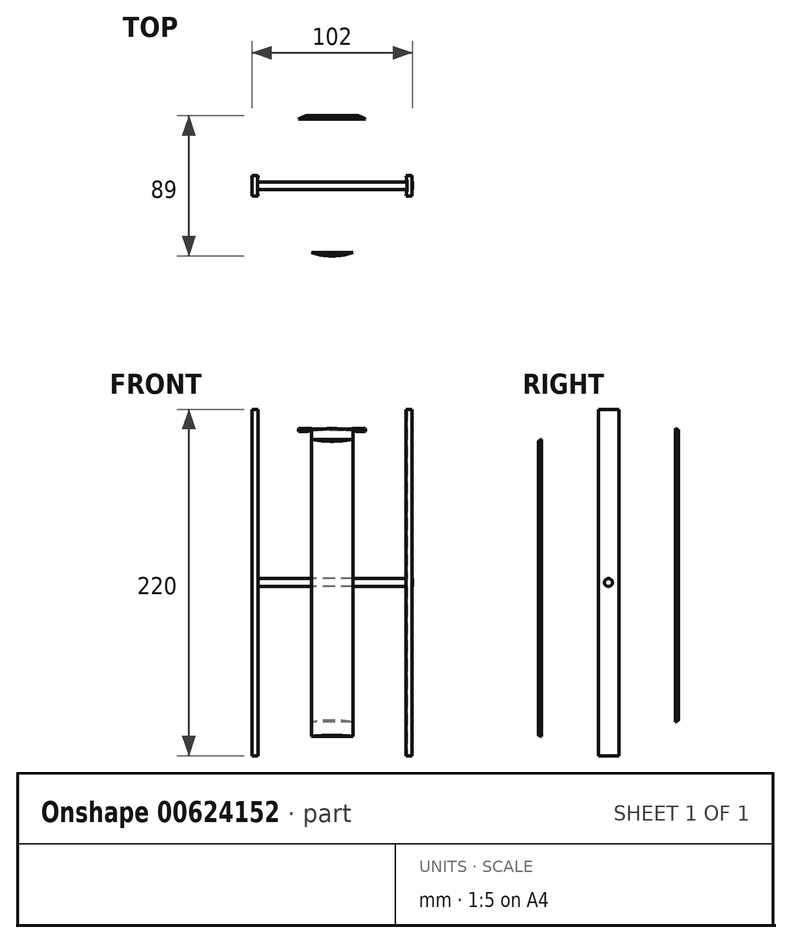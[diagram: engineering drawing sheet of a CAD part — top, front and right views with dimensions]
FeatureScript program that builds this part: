
annotation { "Feature Type Name" : "Feature", "Feature Type Description" : "" }
export const myFeature = defineFeature(function(context is Context, id is Id, definition is map)
    precondition{}
    {
        {
            var Q0;
            Q0=qCreatedBy(makeId("Right.planeOp"),FACE);
            var sketch = newSketch(context, id + "F0", { "sketchPlane" : qUnion([Q0])});
            skLineSegment(sketch, "E0", {"start": v(0, 120.05) * mm, "end": v(0, -127.77) * mm, "construction": true});
            skLineSegment(sketch, "E1", {"start": v(-143.58, 0) * mm, "end": v(127.4, 0) * mm, "construction": true});
            skArc(sketch, "E2", {"start": v(-57.5, 85.46) * mm, "mid": v(-11.29, 102.38) * mm, "end": v(37.5, 95.93) * mm});
            skArc(sketch, "E3.0", {"start": v(-57.5, 87.86) * mm, "mid": v(-11.23, 104.4) * mm, "end": v(37.5, 98.08) * mm});
            skLineSegment(sketch, "E4", {"start": v(-10, -19.22) * mm, "end": v(-10, 530.31) * mm, "construction": true});
            skCircle(sketch, "E5", {"center": v(-10, 215.8) * mm, "radius": 47.5 * mm});
            skLineSegment(sketch, "E6", {"start": v(37.5, -87.86) * mm, "end": v(37.5, -85.46) * mm});
            skLineSegment(sketch, "E7", {"start": v(-57.5, -98.08) * mm, "end": v(-57.5, -95.93) * mm});
            skLineSegment(sketch, "E8", {"start": v(-20, 37.4) * mm, "end": v(-20, -41.37) * mm, "construction": true});
            skArc(sketch, "E9", {"start": v(-57.5, -95.93) * mm, "mid": v(-8.71, -102.38) * mm, "end": v(37.5, -85.46) * mm});
            skArc(sketch, "E10.0", {"start": v(-57.5, -98.08) * mm, "mid": v(-8.77, -104.4) * mm, "end": v(37.5, -87.86) * mm});
            skLineSegment(sketch, "E11", {"start": v(37.5, 104.3) * mm, "end": v(37.5, 301.45) * mm, "construction": true});
            skLineSegment(sketch, "E12", {"start": v(-57.5, 94.09) * mm, "end": v(-57.5, 324.59) * mm, "construction": true});
            skLineSegment(sketch, "E13.trimOffspring", {"start": v(-57.5, 85.46) * mm, "end": v(-57.5, 87.86) * mm});
            skLineSegment(sketch, "E14.trimOffspring", {"start": v(37.5, 95.93) * mm, "end": v(37.5, 98.08) * mm});
            skLineSegment(sketch, "E15", {"start": v(34.5, 97.05) * mm, "end": v(34.5, -87.4) * mm});
            skLineSegment(sketch, "E16", {"start": v(-54.5, 87.4) * mm, "end": v(-54.5, -97.05) * mm});
            skPoint(sketch, "E17.orphan", {"position": v(34.5, 53.9) * mm});
            skPoint(sketch, "E18.orphan", {"position": v(-54.5, 49.75) * mm});
            skLineSegment(sketch, "E19", {"start": v(34.5, -87.4) * mm, "end": v(34.5, -118.04) * mm});
            skLineSegment(sketch, "E20", {"start": v(34.5, -118.04) * mm, "end": v(-54.5, -118.04) * mm});
            skLineSegment(sketch, "E21", {"start": v(-54.5, -118.04) * mm, "end": v(-54.5, -97.05) * mm});
            skLineSegment(sketch, "E22", {"start": v(-54.5, 87.4) * mm, "end": v(-54.5, 114.95) * mm});
            skLineSegment(sketch, "E23", {"start": v(-54.5, 114.95) * mm, "end": v(34.5, 114.95) * mm});
            skLineSegment(sketch, "E24", {"start": v(34.5, 114.95) * mm, "end": v(34.5, 97.05) * mm});
            skLineSegment(sketch, "E25.0", {"start": v(32.5, 114.95) * mm, "end": v(32.5, -118.04) * mm});
            skLineSegment(sketch, "E26.0", {"start": v(-52.5, 114.95) * mm, "end": v(-52.5, -118.04) * mm});
            skCircle(sketch, "E27", {"center": v(-10, 0) * mm, "radius": 2.5 * mm});
            skSolve(sketch);
        }
        {
            var Q0;
            Q0=makeQuery(id+"F0.imprint","IMPRINT",FACE,{"disambiguationData":[TD([[makeQuery(id+"F0.imprint","IMPRINT",EDGE,{"derivedFrom":sQuery(id+"F0.wireOp",EDGE,"E3.0")}),-1.0]])]});
            var Q1;
            {var subQ4=sQuery(id+"F0.wireOp",EDGE,"E6");Q1=makeQuery(id+"F0.imprint","IMPRINT",FACE,{"disambiguationData":[TD([[makeQuery(id+"F0.imprint","IMPRINT",EDGE,{"derivedFrom":subQ4}),1.0]])]});}
            var Q2;
            {var subQ0=sQuery(id+"F0.wireOp",EDGE,"E19");var subQ5=sQuery(id+"F0.wireOp",EDGE,"E10.0");var subQ6=makeQuery(id+"F0.imprint","INTERSECT",VERTEX,{"derivedFrom":[subQ5,subQ0]});Q2=makeQuery(id+"F0.imprint","IMPRINT",FACE,{"disambiguationData":[TD([[makeQuery(id+"F0.imprint","IMPRINT",EDGE,{"disambiguationData":[TD([[subQ6,1.0]])],"derivedFrom":subQ5}),1.0]])]});}
            var Q3;
            {var subQ0=sQuery(id+"F0.wireOp",EDGE,"E26.0");var subQ1=sQuery(id+"F0.wireOp",EDGE,"E9");var subQ2=makeQuery(id+"F0.imprint","INTERSECT",VERTEX,{"derivedFrom":[subQ1,subQ0]});Q3=makeQuery(id+"F0.imprint","IMPRINT",FACE,{"disambiguationData":[TD([[makeQuery(id+"F0.imprint","IMPRINT",EDGE,{"disambiguationData":[TD([[subQ2,-1.0]])],"derivedFrom":subQ1}),-1.0]])]});}
            var Q4;
            {var subQ0=sQuery(id+"F0.wireOp",EDGE,"E7");Q4=makeQuery(id+"F0.imprint","IMPRINT",FACE,{"disambiguationData":[TD([[makeQuery(id+"F0.imprint","IMPRINT",EDGE,{"derivedFrom":subQ0}),-1.0]])]});}
            var Q5;
            {var subQ0=sQuery(id+"F0.wireOp",EDGE,"E21");var subQ5=sQuery(id+"F0.wireOp",EDGE,"E10.0");var subQ6=makeQuery(id+"F0.imprint","INTERSECT",VERTEX,{"derivedFrom":[subQ5,subQ0]});Q5=makeQuery(id+"F0.imprint","IMPRINT",FACE,{"disambiguationData":[TD([[makeQuery(id+"F0.imprint","IMPRINT",EDGE,{"disambiguationData":[TD([[subQ6,-1.0]])],"derivedFrom":subQ5}),1.0]])]});}
            extrude(context, id + "F1", {"entities" : qUnion([Q0, Q1, Q2, Q3, Q4, Q5]), "endBound" : BoundingType.SYMMETRIC, "depth" : 100 * mm, "offsetDistance" : 25 * mm});
        }
        {
            var Q0;
            Q0=qCreatedBy(makeId("Top.planeOp"),FACE);
            var sketch = newSketch(context, id + "F2", { "sketchPlane" : qUnion([Q0])});
            skLineSegment(sketch, "E28.0", {"start": v(0, 37.5) * mm, "end": v(0, -57.5) * mm, "construction": true});
            skCircle(sketch, "E29", {"center": v(0, -10) * mm, "radius": 47.5 * mm});
            skLineSegment(sketch, "E30.bottom", {"start": v(-50.85, -16.52) * mm, "end": v(50.85, -16.52) * mm});
            skLineSegment(sketch, "E30.top", {"start": v(-50.85, -3.48) * mm, "end": v(50.85, -3.48) * mm});
            skLineSegment(sketch, "E30.left", {"start": v(-50.85, -16.52) * mm, "end": v(-50.85, -3.48) * mm});
            skLineSegment(sketch, "E30.right", {"start": v(50.85, -16.52) * mm, "end": v(50.85, -3.48) * mm});
            skSolve(sketch);
        }
        {
            var Q0;
            Q0=makeQuery(id+"F2.imprint","IMPRINT",FACE,{"disambiguationData":[TD([[makeQuery(id+"F2.imprint","IMPRINT",EDGE,{"derivedFrom":sQuery(id+"F2.wireOp",EDGE,"E29")}),1.0]])]});
            var Q1;
            {var subQ0=sQuery(id+"F2.wireOp",EDGE,"E30.bottom");var subQ1=sQuery(id+"F2.wireOp",EDGE,"E29");var subQ2=makeQuery(id+"F2.imprint","INTERSECT",VERTEX,{"disambiguationData":[OD(0.0)],"derivedFrom":[subQ1,subQ0]});Q1=makeQuery(id+"F2.imprint","IMPRINT",FACE,{"disambiguationData":[TD([[makeQuery(id+"F2.imprint","IMPRINT",EDGE,{"disambiguationData":[TD([[subQ2,-1.0]])],"derivedFrom":subQ1}),1.0]])]});}
            var Q2;
            {var subQ0=sQuery(id+"F2.wireOp",EDGE,"E30.top");var subQ1=sQuery(id+"F2.wireOp",EDGE,"E29");var subQ2=makeQuery(id+"F2.imprint","INTERSECT",VERTEX,{"disambiguationData":[OD(0.0)],"derivedFrom":[subQ1,subQ0]});Q2=makeQuery(id+"F2.imprint","IMPRINT",FACE,{"disambiguationData":[TD([[makeQuery(id+"F2.imprint","IMPRINT",EDGE,{"disambiguationData":[TD([[subQ2,1.0]])],"derivedFrom":subQ1}),1.0]])]});}
            extrude(context, id + "F3", {"entities" : qUnion([Q0, Q1, Q2]), "operationType" : NewBodyOperationType.INTERSECT, "endBound" : BoundingType.SYMMETRIC, "depth" : 300 * mm, "offsetDistance" : 25 * mm});
        }
        {
            var Q0;
            {var subQ0=sQuery(id+"F0.wireOp",EDGE,"E24");var subQ1=sQuery(id+"F0.wireOp",EDGE,"E3.0");var subQ2=makeQuery(id+"F0.imprint","INTERSECT",VERTEX,{"derivedFrom":[subQ1,subQ0]});Q0=makeQuery(id+"F0.imprint","IMPRINT",FACE,{"disambiguationData":[TD([[makeQuery(id+"F0.imprint","IMPRINT",EDGE,{"disambiguationData":[TD([[subQ2,1.0]])],"derivedFrom":subQ1}),1.0]])]});}
            var Q1;
            {var subQ0=sQuery(id+"F0.wireOp",EDGE,"E15");Q1=makeQuery(id+"F0.imprint","IMPRINT",FACE,{"disambiguationData":[TD([[makeQuery(id+"F0.imprint","IMPRINT",EDGE,{"derivedFrom":subQ0}),-1.0]])]});}
            var Q2;
            {var subQ0=sQuery(id+"F0.wireOp",EDGE,"E24");var subQ5=sQuery(id+"F0.wireOp",EDGE,"E3.0");var subQ6=makeQuery(id+"F0.imprint","INTERSECT",VERTEX,{"derivedFrom":[subQ5,subQ0]});Q2=makeQuery(id+"F0.imprint","IMPRINT",FACE,{"disambiguationData":[TD([[makeQuery(id+"F0.imprint","IMPRINT",EDGE,{"disambiguationData":[TD([[subQ6,1.0]])],"derivedFrom":subQ5}),-1.0]])]});}
            var Q3;
            {var subQ0=sQuery(id+"F0.wireOp",EDGE,"E19");var subQ5=sQuery(id+"F0.wireOp",EDGE,"E10.0");var subQ6=makeQuery(id+"F0.imprint","INTERSECT",VERTEX,{"derivedFrom":[subQ5,subQ0]});Q3=makeQuery(id+"F0.imprint","IMPRINT",FACE,{"disambiguationData":[TD([[makeQuery(id+"F0.imprint","IMPRINT",EDGE,{"disambiguationData":[TD([[subQ6,1.0]])],"derivedFrom":subQ5}),1.0]])]});}
            var Q4;
            {var subQ0=sQuery(id+"F0.wireOp",EDGE,"E19");var subQ1=sQuery(id+"F0.wireOp",EDGE,"E10.0");var subQ2=makeQuery(id+"F0.imprint","INTERSECT",VERTEX,{"derivedFrom":[subQ1,subQ0]});Q4=makeQuery(id+"F0.imprint","IMPRINT",FACE,{"disambiguationData":[TD([[makeQuery(id+"F0.imprint","IMPRINT",EDGE,{"disambiguationData":[TD([[subQ2,1.0]])],"derivedFrom":subQ1}),-1.0]])]});}
            var Q5;
            Q5=sQuery(id+"F0.wireOp",EDGE,"E4");
            revolve(context, id + "F4", {"entities" : qUnion([Q0, Q1, Q2, Q3, Q4]), "axis" : qUnion([Q5]), "revolveType" : RevolveType.FULL});
        }
        {
            var Q0;
            {var subQ0=sQuery(id+"F0.wireOp",EDGE,"E26.0");var subQ1=sQuery(id+"F0.wireOp",EDGE,"E2");var subQ2=makeQuery(id+"F0.imprint","INTERSECT",VERTEX,{"derivedFrom":[subQ1,subQ0]});Q0=makeQuery(id+"F0.imprint","IMPRINT",FACE,{"disambiguationData":[TD([[makeQuery(id+"F0.imprint","IMPRINT",EDGE,{"disambiguationData":[TD([[subQ2,-1.0]])],"derivedFrom":subQ1}),-1.0]])]});}
            var Q1;
            {var subQ0=sQuery(id+"F0.wireOp",EDGE,"E16");Q1=makeQuery(id+"F0.imprint","IMPRINT",FACE,{"disambiguationData":[TD([[makeQuery(id+"F0.imprint","IMPRINT",EDGE,{"derivedFrom":subQ0}),1.0]])]});}
            var Q2;
            {var subQ0=sQuery(id+"F0.wireOp",EDGE,"E15");Q2=makeQuery(id+"F0.imprint","IMPRINT",FACE,{"disambiguationData":[TD([[makeQuery(id+"F0.imprint","IMPRINT",EDGE,{"derivedFrom":subQ0}),-1.0]])]});}
            var Q3;
            Q3=makeQuery(id+"F0.imprint","IMPRINT",FACE,{"disambiguationData":[TD([[makeQuery(id+"F0.imprint","IMPRINT",EDGE,{"derivedFrom":sQuery(id+"F0.wireOp",EDGE,"E27")}),1.0]])]});
            extrude(context, id + "F5", {"entities" : qUnion([Q0, Q1, Q2, Q3]), "operationType" : NewBodyOperationType.INTERSECT, "endBound" : BoundingType.SYMMETRIC, "depth" : 100 * mm, "offsetDistance" : 25 * mm});
        }
        {
            var Q0;
            {var subQ5=sQuery(id+"F2.wireOp",EDGE,"E30.left");Q0=makeQuery(id+"F2.imprint","IMPRINT",FACE,{"disambiguationData":[TD([[makeQuery(id+"F2.imprint","IMPRINT",EDGE,{"derivedFrom":subQ5}),-1.0]])]});}
            var Q1;
            {var subQ5=sQuery(id+"F2.wireOp",EDGE,"E30.right");Q1=makeQuery(id+"F2.imprint","IMPRINT",FACE,{"disambiguationData":[TD([[makeQuery(id+"F2.imprint","IMPRINT",EDGE,{"derivedFrom":subQ5}),1.0]])]});}
            extrude(context, id + "F6", {"entities" : qUnion([Q0, Q1]), "operationType" : NewBodyOperationType.ADD, "endBound" : BoundingType.SYMMETRIC, "depth" : 220 * mm, "offsetDistance" : 25 * mm});
        }
        {
            var Q0;
            Q0=makeQuery(id+"F0.imprint","IMPRINT",FACE,{"disambiguationData":[TD([[makeQuery(id+"F0.imprint","IMPRINT",EDGE,{"derivedFrom":sQuery(id+"F0.wireOp",EDGE,"E27")}),1.0]])]});
            extrude(context, id + "F7", {"entities" : qUnion([Q0]), "operationType" : NewBodyOperationType.REMOVE, "endBound" : BoundingType.SYMMETRIC, "oppositeDirection" : true, "depth" : 180 * mm, "offsetDistance" : 25 * mm});
        }
        {
            var Q0;
            Q0=makeQuery(id+"F0.imprint","IMPRINT",FACE,{"disambiguationData":[TD([[makeQuery(id+"F0.imprint","IMPRINT",EDGE,{"derivedFrom":sQuery(id+"F0.wireOp",EDGE,"E27")}),1.0]])]});
            extrude(context, id + "F8", {"entities" : qUnion([Q0]), "operationType" : NewBodyOperationType.ADD, "endBound" : BoundingType.SYMMETRIC, "depth" : 102 * mm, "offsetDistance" : 25 * mm});
        }
    });
